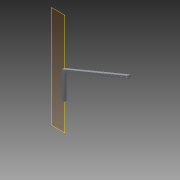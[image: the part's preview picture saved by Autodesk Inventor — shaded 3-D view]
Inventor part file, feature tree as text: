
AUTODESK INVENTOR PART (.ipt)
format: ipt  version: 2013 (Build 170138000, 138)  size: 98,816 bytes
history: native  units: in
note: dims shown in document units (in); Inventor stores cm internally (conversion verified against a paired STEP export)
features: plane x1, extrude x1, sketch x1
ambient origin geometry x8: Origin, YZ Plane, XZ Plane, XY Plane, X Axis, Y Axis, Z Axis, Center Point
bodies: Solid1 (feature_tree)
feature tree (3):
  plane  "Work Plane1"
  extrude  "Extrusion1"  Depth=19.0in
  sketch  "Sketch1"  dims[d0=2.5in d1=19.0in d2=5.0in d3=3.0in d4=7.0in d5=90.0deg d6=53.0in d7=7.0in d10=0.5in d11=0.5in d13=0.75in d14=22.5deg d15=0.5in d16=1.0in d17=90.0deg d18=157.5deg d19=10.0in d20=1.0in d21=90.0deg d22=1.0in d23=0.0in d24=1.0in d25=0.0in]
